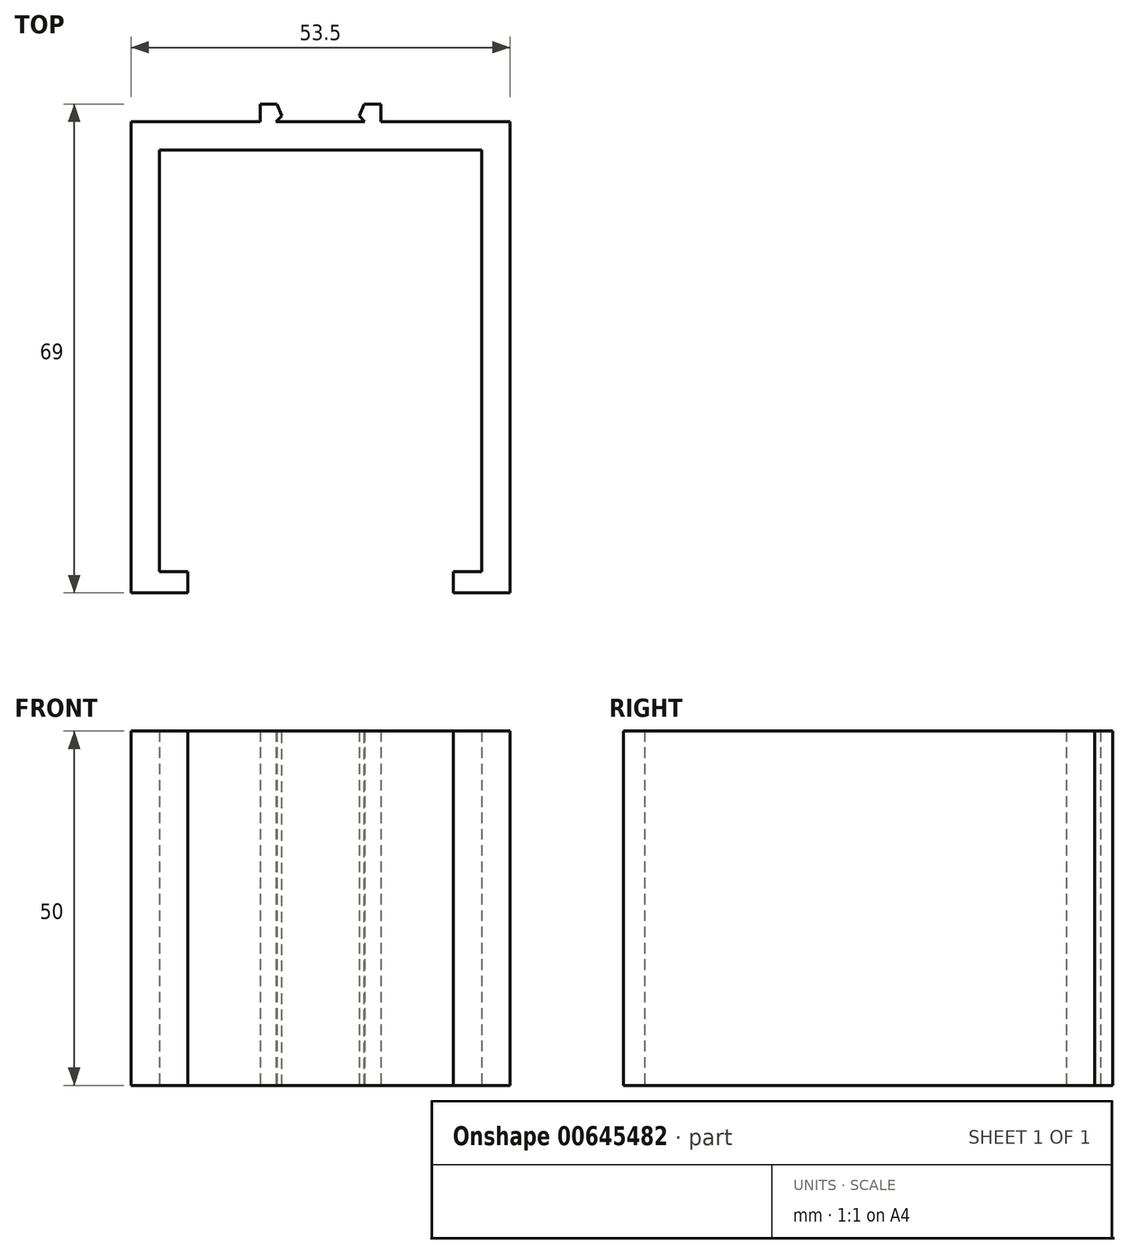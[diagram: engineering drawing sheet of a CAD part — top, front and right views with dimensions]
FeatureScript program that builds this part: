
annotation { "Feature Type Name" : "Feature", "Feature Type Description" : "" }
export const myFeature = defineFeature(function(context is Context, id is Id, definition is map)
    precondition{}
    {
        {
            var Q0;
            Q0=qCreatedBy(makeId("Top.planeOp"),FACE);
            var sketch = newSketch(context, id + "F0", { "sketchPlane" : qUnion([Q0])});
            skLineSegment(sketch, "E0.bottom", {"start": v(0, 0) * mm, "end": v(-45.5, 0) * mm});
            skLineSegment(sketch, "E0.top", {"start": v(0, -59.5) * mm, "end": v(-4, -59.5) * mm});
            skLineSegment(sketch, "E0.left", {"start": v(0, 0) * mm, "end": v(0, -59.5) * mm});
            skLineSegment(sketch, "E0.right", {"start": v(-45.5, 0) * mm, "end": v(-45.5, -59.5) * mm});
            skLineSegment(sketch, "E1.bottom", {"start": v(-49.5, 4) * mm, "end": v(4, 4) * mm});
            skLineSegment(sketch, "E1.top", {"start": v(-49.5, -62.5) * mm, "end": v(-41.5, -62.5) * mm});
            skLineSegment(sketch, "E1.left", {"start": v(-49.5, 4) * mm, "end": v(-49.5, -62.5) * mm});
            skLineSegment(sketch, "E1.right", {"start": v(4, 4) * mm, "end": v(4, -62.5) * mm});
            skLineSegment(sketch, "E2", {"start": v(-41.5, -59.5) * mm, "end": v(-41.5, -62.5) * mm});
            skLineSegment(sketch, "E3", {"start": v(-4, -59.5) * mm, "end": v(-4, -62.5) * mm});
            skLineSegment(sketch, "E4.trimOffspring", {"start": v(-41.5, -59.5) * mm, "end": v(-45.5, -59.5) * mm});
            skLineSegment(sketch, "E5.trimOffspring", {"start": v(-4, -62.5) * mm, "end": v(4, -62.5) * mm});
            skLineSegment(sketch, "E6", {"start": v(-31.25, 4) * mm, "end": v(-31.25, 6.5) * mm});
            skLineSegment(sketch, "E7", {"start": v(-31.25, 6.5) * mm, "end": v(-26.5, 6.5) * mm});
            skLineSegment(sketch, "E8", {"start": v(-26.5, 6.5) * mm, "end": v(-29, 4) * mm});
            skLineSegment(sketch, "E9", {"start": v(-16.5, 4) * mm, "end": v(-19, 6.5) * mm});
            skLineSegment(sketch, "E10", {"start": v(-19, 6.5) * mm, "end": v(-14.25, 6.5) * mm});
            skLineSegment(sketch, "E11", {"start": v(-14.25, 6.5) * mm, "end": v(-14.25, 4) * mm});
            skSolve(sketch);
        }
        {
            var Q0;
            Q0 = qSketchRegion(id + "F0", true);
            extrude(context, id + "F1", {"entities" : qUnion([Q0]), "depth" : 50 * mm, "offsetDistance" : 25 * mm});
        }
        {
            var Q0;
            Q0=makeQuery(id+"F1.opExtrude","SWEPT_EDGE",EDGE,{"disambiguationData":[OSD([sQuery(id+"F0.wireOp",EDGE,"E9"),sQuery(id+"F0.wireOp",EDGE,"E10")])]});
            var Q1;
            Q1=makeQuery(id+"F1.opExtrude","SWEPT_EDGE",EDGE,{"disambiguationData":[OSD([sQuery(id+"F0.wireOp",EDGE,"E7"),sQuery(id+"F0.wireOp",EDGE,"E8")])]});
            chamfer(context, id + "F2", {"entities" : qUnion([Q0, Q1]), "width" : 1 * mm, "tangentPropagation" : true});
        }
    });
